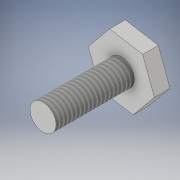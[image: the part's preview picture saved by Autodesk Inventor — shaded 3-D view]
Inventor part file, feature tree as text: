
AUTODESK INVENTOR PART (.ipt)
format: ipt  version: 2019 (Build 230136000, 136)  size: 107,520 bytes
history: native  units: mm
features: extrude x2, sketch x2, thread x1
ambient origin geometry x8: Origin, YZ Plane, XZ Plane, XY Plane, X Axis, Y Axis, Z Axis, Center Point
bodies: Solid1 (feature_tree)
feature tree (5):
  extrude  "Extrusion1"  Depth=3.0mm
  extrude  "Extrusion2"  Depth=10.0mm TaperAngle=0.0deg
  thread  "Thread1"  [1 undecoded]
  sketch  "Sketch1"  dims[d0=3.0mm d1=0.0mm d2=5.0mm]
  sketch  "Sketch2"  dims[d3=15.0mm d4=0.0mm d5=10.0mm d6=0.0mm]
note: 1 required parameter value undecoded (feature->parameter linkage not recoverable at this tier; creation-order binding heuristic only, values carry confidence <= 0.55)
